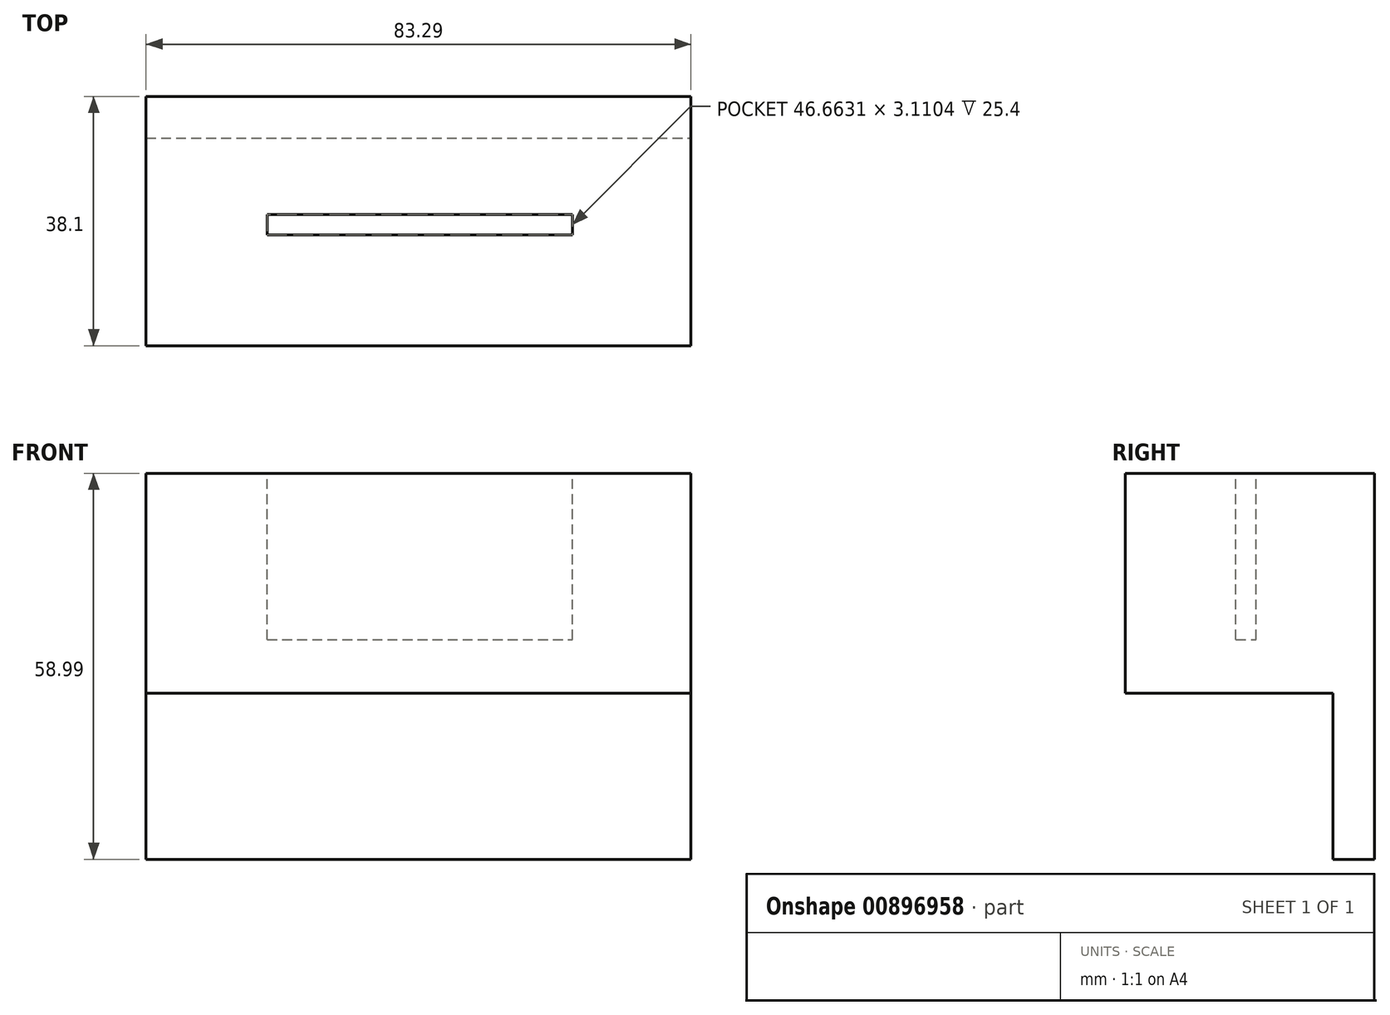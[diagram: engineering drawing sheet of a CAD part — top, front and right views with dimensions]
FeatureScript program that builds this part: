
annotation { "Feature Type Name" : "Feature", "Feature Type Description" : "" }
export const myFeature = defineFeature(function(context is Context, id is Id, definition is map)
    precondition{}
    {
        {
            var Q0;
            Q0=qCreatedBy(makeId("Front.planeOp"),FACE);
            var sketch = newSketch(context, id + "F0", { "sketchPlane" : qUnion([Q0])});
            skLineSegment(sketch, "E0.bottom", {"start": v(-30.1, 35.57) * mm, "end": v(53.18, 35.57) * mm});
            skLineSegment(sketch, "E0.top", {"start": v(-30.1, 1.98) * mm, "end": v(53.18, 1.98) * mm});
            skLineSegment(sketch, "E0.left", {"start": v(-30.1, 35.57) * mm, "end": v(-30.1, 1.98) * mm});
            skLineSegment(sketch, "E0.right", {"start": v(53.18, 35.57) * mm, "end": v(53.18, 1.98) * mm});
            skFitSpline(sketch, "E1", {"points": [v(-19.18, 1.98) * mm, v(-18.91, -16.73) * mm], "startDerivative": vector(0.27, -18.7) * mm, "endDerivative": vector(0.27, -18.7) * mm});
            skFitSpline(sketch, "E2", {"points": [v(-18.91, -16.73) * mm, v(-9.49, -16.73) * mm], "startDerivative": vector(9.42, 0) * mm, "endDerivative": vector(9.42, 0) * mm});
            skFitSpline(sketch, "E3", {"points": [v(-9.49, -16.73) * mm, v(-9.49, -7.85) * mm, v(-9.49, 1.98) * mm], "startDerivative": vector(0, 17.98) * mm, "endDerivative": vector(0, 19.42) * mm});
            skSolve(sketch);
        }
        {
            var Q0;
            Q0=makeQuery(id+"F0.imprint","IMPRINT",FACE,{"disambiguationData":[TD([[makeQuery(id+"F0.imprint","IMPRINT",EDGE,{"derivedFrom":sQuery(id+"F0.wireOp",EDGE,"E0.bottom")}),-1.0]])]});
            var Q1;
            Q1 = qSketchRegion(id + "F2", true);
            extrude(context, id + "F1", {"entities" : qUnion([Q0, Q1]), "oppositeDirection" : true, "depth" : 38.1 * mm, "offsetDistance" : 25.4 * mm});
        }
        {
            var Q0;
            Q0=makeQuery(id+"F1.opExtrude","CAP_FACE",FACE,{"disambiguationData":[OSD([sQuery(id+"F0.wireOp",EDGE,"E0.bottom"),sQuery(id+"F0.wireOp",EDGE,"E0.top"),sQuery(id+"F0.wireOp",EDGE,"E0.left"),sQuery(id+"F0.wireOp",EDGE,"E0.right")])],"isStart":false});
            var sketch = newSketch(context, id + "F2", { "sketchPlane" : qUnion([Q0])});
            skLineSegment(sketch, "E4.bottom", {"start": v(-53.18, 35.57) * mm, "end": v(30.1, 35.57) * mm});
            skLineSegment(sketch, "E4.top", {"start": v(-53.18, -23.42) * mm, "end": v(30.1, -23.42) * mm});
            skLineSegment(sketch, "E4.left", {"start": v(30.1, -23.42) * mm, "end": v(30.1, 35.57) * mm});
            skLineSegment(sketch, "E4.right", {"start": v(-53.18, -23.42) * mm, "end": v(-53.18, 35.57) * mm});
            skSolve(sketch);
        }
        {
            var Q0;
            {var subQ0=sQuery(id+"F2.wireOp",EDGE,"E4.bottom");Q0=makeQuery(id+"F2.imprint","IMPRINT",FACE,{"disambiguationData":[TD([[makeQuery(id+"F2.imprint","IMPRINT",EDGE,{"derivedFrom":subQ0}),-1.0]])]});}
            var Q1;
            {var subQ0=sQuery(id+"F2.wireOp",EDGE,"E4.top");Q1=makeQuery(id+"F2.imprint","IMPRINT",FACE,{"disambiguationData":[TD([[makeQuery(id+"F2.imprint","IMPRINT",EDGE,{"derivedFrom":subQ0}),1.0]])]});}
            extrude(context, id + "F3", {"entities" : qUnion([Q0, Q1]), "operationType" : NewBodyOperationType.ADD, "oppositeDirection" : true, "depth" : 6.35 * mm, "offsetDistance" : 25.4 * mm});
        }
        {
            var Q0;
            Q0=makeQuery(id+"F1.opExtrude","SWEPT_FACE",FACE,{"disambiguationData":[OSD([sQuery(id+"F0.wireOp",EDGE,"E0.bottom")])]});
            var sketch = newSketch(context, id + "F4", { "sketchPlane" : qUnion([Q0])});
            skLineSegment(sketch, "E5.bottom", {"start": v(-11.59, 16.9) * mm, "end": v(35.08, 16.9) * mm});
            skLineSegment(sketch, "E5.top", {"start": v(-11.59, 20.01) * mm, "end": v(35.08, 20.01) * mm});
            skLineSegment(sketch, "E5.left", {"start": v(-11.59, 16.9) * mm, "end": v(-11.59, 20.01) * mm});
            skLineSegment(sketch, "E5.right", {"start": v(35.08, 16.9) * mm, "end": v(35.08, 20.01) * mm});
            skSolve(sketch);
        }
        {
            var Q0;
            Q0 = qSketchRegion(id + "F4", true);
            extrude(context, id + "F5", {"entities" : qUnion([Q0]), "operationType" : NewBodyOperationType.REMOVE, "oppositeDirection" : true, "depth" : 25.4 * mm, "offsetDistance" : 25.4 * mm});
        }
    });
